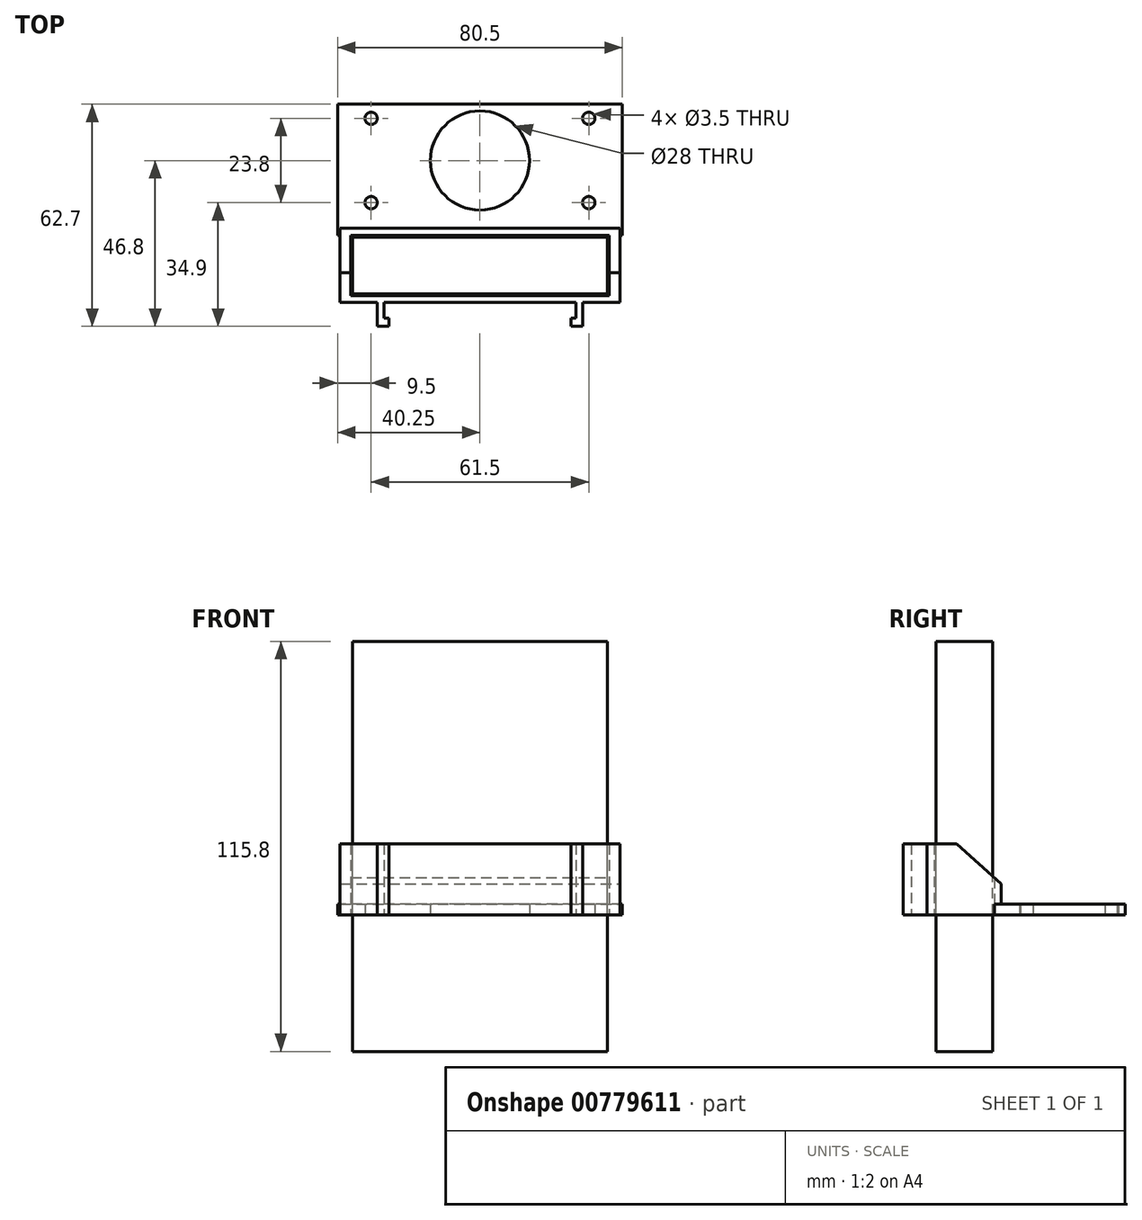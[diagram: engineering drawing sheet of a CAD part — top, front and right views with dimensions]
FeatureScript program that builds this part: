
annotation { "Feature Type Name" : "Feature", "Feature Type Description" : "" }
export const myFeature = defineFeature(function(context is Context, id is Id, definition is map)
    precondition{}
    {
        {
            var Q0;
            Q0=qCreatedBy(makeId("Top.planeOp"),FACE);
            var sketch = newSketch(context, id + "F0", { "sketchPlane" : qUnion([Q0])});
            skLineSegment(sketch, "E0.bottom", {"start": v(40.25, 18.5) * mm, "end": v(-40.25, 18.5) * mm});
            skLineSegment(sketch, "E0.top", {"start": v(40.25, -18.5) * mm, "end": v(-40.25, -18.5) * mm});
            skLineSegment(sketch, "E0.left", {"start": v(40.25, 18.5) * mm, "end": v(40.25, -18.5) * mm});
            skLineSegment(sketch, "E0.right", {"start": v(-40.25, 18.5) * mm, "end": v(-40.25, -18.5) * mm});
            skPoint(sketch, "E0.middle", {"position": v(0, 0) * mm});
            skCircle(sketch, "E1", {"center": v(-30.75, 14.5) * mm, "radius": 1.75 * mm});
            skCircle(sketch, "E2", {"center": v(-30.75, -9.3) * mm, "radius": 1.75 * mm});
            skCircle(sketch, "E3", {"center": v(30.75, -9.3) * mm, "radius": 1.75 * mm});
            skCircle(sketch, "E4", {"center": v(30.75, 14.5) * mm, "radius": 1.75 * mm});
            skSolve(sketch);
        }
        {
            var Q0;
            Q0 = qSketchRegion(id + "F0", true);
            extrude(context, id + "F1", {"entities" : qUnion([Q0]), "depth" : 3 * mm, "offsetDistance" : 25 * mm});
        }
        {
            var Q0;
            Q0=qCreatedBy(makeId("Top.planeOp"),FACE);
            var sketch = newSketch(context, id + "F2", { "sketchPlane" : qUnion([Q0])});
            skLineSegment(sketch, "E5.bottom", {"start": v(36.5, -18.5) * mm, "end": v(-36.5, -18.5) * mm});
            skLineSegment(sketch, "E5.top", {"start": v(36.5, -35.5) * mm, "end": v(-36.5, -35.5) * mm});
            skLineSegment(sketch, "E5.left", {"start": v(36.5, -18.5) * mm, "end": v(36.5, -35.5) * mm});
            skLineSegment(sketch, "E5.right", {"start": v(-36.5, -18.5) * mm, "end": v(-36.5, -35.5) * mm});
            skPoint(sketch, "E5.middle", {"position": v(0, -27) * mm});
            skLineSegment(sketch, "E6.0", {"start": v(39.5, -16.5) * mm, "end": v(-39.5, -16.5) * mm});
            skLineSegment(sketch, "E6.2", {"start": v(39.5, -37.5) * mm, "end": v(-39.5, -37.5) * mm});
            skLineSegment(sketch, "E7.0", {"start": v(40.25, -18.5) * mm, "end": v(-40.25, -18.5) * mm, "construction": true});
            skLineSegment(sketch, "E8", {"start": v(39.5, -16.5) * mm, "end": v(39.5, -37.5) * mm});
            skLineSegment(sketch, "E9", {"start": v(-39.5, -16.5) * mm, "end": v(-39.5, -37.5) * mm});
            skLineSegment(sketch, "E10", {"start": v(29, -37.5) * mm, "end": v(29, -44.2) * mm});
            skLineSegment(sketch, "E11", {"start": v(29, -44.2) * mm, "end": v(25.75, -44.2) * mm});
            skLineSegment(sketch, "E12", {"start": v(25.75, -44.2) * mm, "end": v(25.75, -41.9) * mm});
            skLineSegment(sketch, "E13", {"start": v(25.75, -41.9) * mm, "end": v(27.1, -41.9) * mm});
            skLineSegment(sketch, "E14", {"start": v(27.1, -41.9) * mm, "end": v(27.1, -37.5) * mm});
            skLineSegment(sketch, "E15.MirrorCS", {"start": v(-29, -37.5) * mm, "end": v(-29, -44.2) * mm});
            skLineSegment(sketch, "E16.MirrorCS", {"start": v(-27.1, -41.9) * mm, "end": v(-27.1, -37.5) * mm});
            skLineSegment(sketch, "E17.MirrorCS", {"start": v(-25.75, -41.9) * mm, "end": v(-27.1, -41.9) * mm});
            skLineSegment(sketch, "E18.MirrorCS", {"start": v(-25.75, -44.2) * mm, "end": v(-25.75, -41.9) * mm});
            skLineSegment(sketch, "E19.MirrorCS", {"start": v(-29, -44.2) * mm, "end": v(-25.75, -44.2) * mm});
            skSolve(sketch);
        }
        {
            var Q0;
            Q0=makeQuery(id+"F2.imprint","IMPRINT",FACE,{"disambiguationData":[TD([[makeQuery(id+"F2.imprint","IMPRINT",EDGE,{"derivedFrom":sQuery(id+"F2.wireOp",EDGE,"E5.bottom")}),-1.0]])]});
            var Q1;
            {var subQ0=sQuery(id+"F2.wireOp",EDGE,"E15.MirrorCS");Q1=makeQuery(id+"F2.imprint","IMPRINT",FACE,{"disambiguationData":[TD([[makeQuery(id+"F2.imprint","IMPRINT",EDGE,{"derivedFrom":subQ0}),1.0]])]});}
            var Q2;
            {var subQ0=sQuery(id+"F2.wireOp",EDGE,"E10");Q2=makeQuery(id+"F2.imprint","IMPRINT",FACE,{"disambiguationData":[TD([[makeQuery(id+"F2.imprint","IMPRINT",EDGE,{"derivedFrom":subQ0}),-1.0]])]});}
            extrude(context, id + "F3", {"entities" : qUnion([Q0, Q1, Q2]), "operationType" : NewBodyOperationType.ADD, "depth" : 20 * mm, "offsetDistance" : 25 * mm});
        }
        {
            var Q0;
            Q0=makeQuery(id+"F3.opExtrude","SWEPT_FACE",FACE,{"disambiguationData":[OSD([sQuery(id+"F2.wireOp",EDGE,"E8")])]});
            var sketch = newSketch(context, id + "F4", { "sketchPlane" : qUnion([Q0])});
            skLineSegment(sketch, "E20.0", {"start": v(-16.5, 20) * mm, "end": v(-16.5, 3) * mm});
            skLineSegment(sketch, "E21", {"start": v(-29.1, 20) * mm, "end": v(-16.5, 8.7) * mm});
            skSolve(sketch);
        }
        {
            var Q0;
            {var subQ3=sQuery(id+"F4.wireOp",EDGE,"E21");Q0=makeQuery(id+"F4.imprint","IMPRINT",FACE,{"disambiguationData":[TD([[makeQuery(id+"F4.imprint","IMPRINT",EDGE,{"derivedFrom":subQ3}),1.0]])]});}
            var Q1;
            Q1=makeQuery(id+"F3.opExtrude","SWEPT_FACE",FACE,{"disambiguationData":[OSD([sQuery(id+"F2.wireOp",EDGE,"E9")])]});
            extrude(context, id + "F5", {"entities" : qUnion([Q0]), "operationType" : NewBodyOperationType.REMOVE, "endBound" : BoundingType.UP_TO_SURFACE, "oppositeDirection" : true, "depth" : 25 * mm, "endBoundEntityFace" : qUnion([Q1]), "offsetDistance" : 25 * mm});
        }
        {
            var Q0;
            Q0=makeQuery(id+"F3.boolean.opBoolean","MERGE",FACE,{"derivedFrom":[makeQuery(id+"F1.opExtrude","CAP_FACE",FACE,{"disambiguationData":[OSD([sQuery(id+"F0.wireOp",EDGE,"E0.bottom"),sQuery(id+"F0.wireOp",EDGE,"E0.top"),sQuery(id+"F0.wireOp",EDGE,"E0.left"),sQuery(id+"F0.wireOp",EDGE,"E0.right"),sQuery(id+"F0.wireOp",EDGE,"E1"),sQuery(id+"F0.wireOp",EDGE,"E2"),sQuery(id+"F0.wireOp",EDGE,"E3"),sQuery(id+"F0.wireOp",EDGE,"E4")])],"isStart":true}),makeQuery(id+"F3.opExtrude","CAP_FACE",FACE,{"disambiguationData":[OSD([sQuery(id+"F2.wireOp",EDGE,"E5.bottom"),sQuery(id+"F2.wireOp",EDGE,"E5.top"),sQuery(id+"F2.wireOp",EDGE,"E5.left"),sQuery(id+"F2.wireOp",EDGE,"E5.right"),sQuery(id+"F2.wireOp",EDGE,"E6.0"),sQuery(id+"F2.wireOp",EDGE,"E6.1"),sQuery(id+"F2.wireOp",EDGE,"E6.2"),sQuery(id+"F2.wireOp",EDGE,"E6.3")])],"isStart":true})]});
            var sketch = newSketch(context, id + "F6", { "sketchPlane" : qUnion([Q0])});
            skCircle(sketch, "E22", {"center": v(0, -2.6) * mm, "radius": 14 * mm});
            skSolve(sketch);
        }
        {
            var Q0;
            Q0 = qSketchRegion(id + "F6", true);
            extrude(context, id + "F7", {"entities" : qUnion([Q0]), "operationType" : NewBodyOperationType.REMOVE, "oppositeDirection" : true, "depth" : 25 * mm, "offsetDistance" : 25 * mm});
        }
        {
            var Q0;
            Q0=makeQuery(id+"F1.opExtrude","CAP_FACE",FACE,{"disambiguationData":[OSD([sQuery(id+"F0.wireOp",EDGE,"E0.bottom"),sQuery(id+"F0.wireOp",EDGE,"E0.top"),sQuery(id+"F0.wireOp",EDGE,"E0.left"),sQuery(id+"F0.wireOp",EDGE,"E0.right"),sQuery(id+"F0.wireOp",EDGE,"E1"),sQuery(id+"F0.wireOp",EDGE,"E2"),sQuery(id+"F0.wireOp",EDGE,"E3"),sQuery(id+"F0.wireOp",EDGE,"E4")])],"isStart":false});
            var sketch = newSketch(context, id + "F8", { "sketchPlane" : qUnion([Q0])});
            skCircle(sketch, "E23.0", {"center": v(30.75, -9.3) * mm, "radius": 3.15 * mm});
            skCircle(sketch, "E24.0", {"center": v(-30.75, -9.3) * mm, "radius": 3.15 * mm});
            skSolve(sketch);
        }
        {
            var Q0;
            Q0 = qSketchRegion(id + "F8", true);
            extrude(context, id + "F9", {"entities" : qUnion([Q0]), "operationType" : NewBodyOperationType.REMOVE, "depth" : 25 * mm, "offsetDistance" : 25 * mm});
        }
        {
            var Q0;
            Q0=makeQuery(id+"F3.boolean.opBoolean","MERGE",FACE,{"derivedFrom":[makeQuery(id+"F1.opExtrude","CAP_FACE",FACE,{"disambiguationData":[OSD([sQuery(id+"F0.wireOp",EDGE,"E0.bottom"),sQuery(id+"F0.wireOp",EDGE,"E0.top"),sQuery(id+"F0.wireOp",EDGE,"E0.left"),sQuery(id+"F0.wireOp",EDGE,"E0.right"),sQuery(id+"F0.wireOp",EDGE,"E1"),sQuery(id+"F0.wireOp",EDGE,"E2"),sQuery(id+"F0.wireOp",EDGE,"E3"),sQuery(id+"F0.wireOp",EDGE,"E4")])],"isStart":true}),makeQuery(id+"F3.opExtrude","CAP_FACE",FACE,{"disambiguationData":[OSD([sQuery(id+"F2.wireOp",EDGE,"E5.bottom"),sQuery(id+"F2.wireOp",EDGE,"E5.top"),sQuery(id+"F2.wireOp",EDGE,"E5.left"),sQuery(id+"F2.wireOp",EDGE,"E5.right"),sQuery(id+"F2.wireOp",EDGE,"E6.0"),sQuery(id+"F2.wireOp",EDGE,"E6.2"),sQuery(id+"F2.wireOp",EDGE,"E8"),sQuery(id+"F2.wireOp",EDGE,"E9"),sQuery(id+"F2.wireOp",EDGE,"E10"),sQuery(id+"F2.wireOp",EDGE,"E11"),sQuery(id+"F2.wireOp",EDGE,"E12"),sQuery(id+"F2.wireOp",EDGE,"E13"),sQuery(id+"F2.wireOp",EDGE,"E14"),sQuery(id+"F2.wireOp",EDGE,"E15.MirrorCS"),sQuery(id+"F2.wireOp",EDGE,"E16.MirrorCS"),sQuery(id+"F2.wireOp",EDGE,"E17.MirrorCS"),sQuery(id+"F2.wireOp",EDGE,"E18.MirrorCS"),sQuery(id+"F2.wireOp",EDGE,"E19.MirrorCS")])],"isStart":true})]});
            var sketch = newSketch(context, id + "F10", { "sketchPlane" : qUnion([Q0])});
            skLineSegment(sketch, "E25.0", {"start": v(36.5, 18.5) * mm, "end": v(-36.5, 18.5) * mm, "construction": true});
            skLineSegment(sketch, "E26.0", {"start": v(36.5, 18.5) * mm, "end": v(36.5, 35.5) * mm, "construction": true});
            skLineSegment(sketch, "E27.0", {"start": v(36.5, 35.5) * mm, "end": v(-36.5, 35.5) * mm, "construction": true});
            skLineSegment(sketch, "E28.0", {"start": v(-36.5, 18.5) * mm, "end": v(-36.5, 35.5) * mm, "construction": true});
            skLineSegment(sketch, "E29.0", {"start": v(36, 19) * mm, "end": v(-36, 19) * mm});
            skLineSegment(sketch, "E29.1", {"start": v(36, 19) * mm, "end": v(36, 35) * mm});
            skLineSegment(sketch, "E29.2", {"start": v(36, 35) * mm, "end": v(-36, 35) * mm});
            skLineSegment(sketch, "E29.3", {"start": v(-36, 19) * mm, "end": v(-36, 35) * mm});
            skSolve(sketch);
        }
        {
            var Q0;
            Q0 = qSketchRegion(id + "F10", true);
            extrude(context, id + "F11", {"entities" : qUnion([Q0]), "depth" : 38.6 * mm, "offsetDistance" : 25 * mm, "hasSecondDirection" : true, "secondDirectionOppositeDirection" : true, "secondDirectionDepth" : 77.2 * mm});
        }
    });
